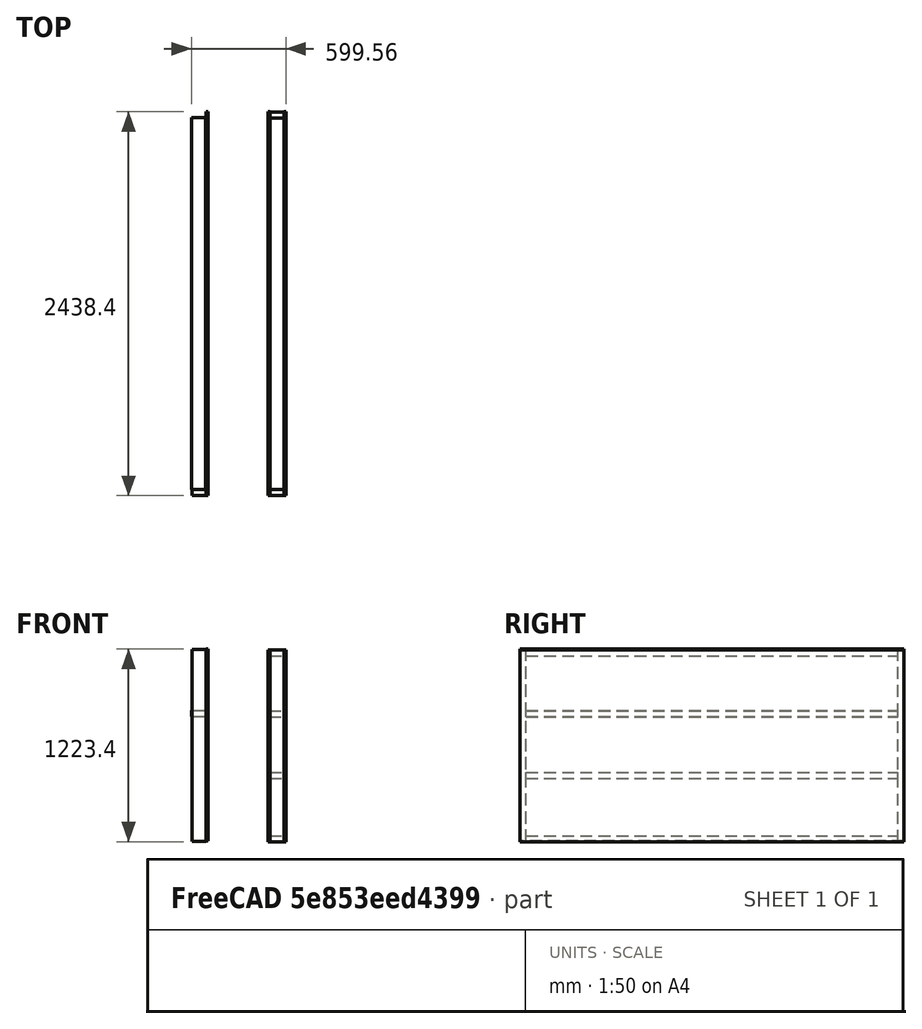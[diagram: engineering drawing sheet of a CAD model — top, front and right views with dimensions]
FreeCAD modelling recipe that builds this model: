
FCSTD DOCUMENT  (FreeCAD 0.17R13125 (Git))
Label: case
License: All rights reserved
LicenseURL: http://en.wikipedia.org/wiki/All_rights_reserved
objects: Part::FeaturePython×6, Part::Box×3
note: 9 computed .brp shape members not serialized (recipe doc carries the construction recipe); baked Part::Feature solids carry a one-line shape summary decoded from their .brp

FEATURE [Part::Box] Box  label="Cube"
  AttacherType = Attacher::AttachEngine3D
  Height = 2438.4
  Length = 12.7
  Placement = pos=(0,574.666,-716.368) rot=(1,0,0;1.5708rad)
  Width = 1219.2
FEATURE [Part::Box] Box001  label="Cube001"
  AttacherType = Attacher::AttachEngine3D
  Height = 38.1
  Length = 88.9
  Placement = pos=(12.2326,-1825.56,464.739) rot=(0,0,1;0rad)
  Width = 2362.2
FEATURE [Part::FeaturePython] Clone  label="Cube002"  # Draft clone (typed FeaturePython)
  AttacherType = Attacher::AttachEngine3D
  Fuse = false
  Objects = -> [Box001]
  Placement = pos=(12.7605,-1825.56,-715.956) rot=(0,0,1;0rad)
  Scale = (1,1,1)
FEATURE [Part::FeaturePython] Clone002  label="Cube004"  # Draft clone (typed FeaturePython)
  AttacherType = Attacher::AttachEngine3D
  Fuse = false
  Objects = -> [Clone]
  Placement = pos=(13.3426,-1825.56,-314.867) rot=(0,0,1;0rad)
  Scale = (1,1,1)
FEATURE [Part::FeaturePython] Clone003  label="Cube005"  # Draft clone (typed FeaturePython)
  AttacherType = Attacher::AttachEngine3D
  Fuse = false
  Objects = -> [Clone002]
  Placement = pos=(9.2831,-1825.56,75.4186) rot=(0,0,1;0rad)
  Scale = (1,1,1)
FEATURE [Part::Box] Box002  label="Cube006"
  AttacherType = Attacher::AttachEngine3D
  Height = 1219.2
  Length = 38.1
  Placement = pos=(101.576,535.919,-716.263) rot=(0,0,1;1.5708rad)
  Width = 88.9
FEATURE [Part::FeaturePython] Clone004  label="Cube007"  # Draft clone (typed FeaturePython)
  AttacherType = Attacher::AttachEngine3D
  Fuse = false
  Objects = -> [Box002]
  Placement = pos=(101.458,-1863.48,-716.263) rot=(0,0,1;1.5708rad)
  Scale = (1,1,1)
FEATURE [Part::FeaturePython] Clone005  label="Cube008"  # Draft clone (typed FeaturePython)
  AttacherType = Attacher::AttachEngine3D
  Fuse = false
  Objects = -> [Box]
  Placement = pos=(101.802,574.666,-716.004) rot=(1,0,0;1.5708rad)
  Scale = (1,1,1)
FEATURE [Part::FeaturePython] Clone014  label="Compound001"  # WARN: FeaturePython — macro-defined, semantics opaque (R4)
  AttacherType = Attacher::AttachEngine3D
  Fuse = false
  Placement = pos=(494.337,-2.28411e-07,-3.83209) rot=(0,0,1;0rad)
  Scale = (1,1,1)
